# Revit family: Rohrschelle Omnia, M10, Gummi
name_source: partatom
category: HLS-Bauteile
revit_build: Autodesk Revit 2017 (Build: 20190507_1515(x64)
units: mm (PartAtom-declared; Revit-internal decimal feet)

## family parameters
Arbeitsebenenbasiert = Ja
Beim Laden mit Abzugskörper schneiden = Nein
Bemaßung runder Anschluss = Durchmesser verwenden
Gemeinsam genutzt = Ja
Immer vertikal = Nein
Raumberechnungspunkt = Nein
Teiletyp = Normal

## types (10) — shared parameters
Anschluss = M10
BP = 14 mm  [stored 0.0459318 ft]
Bauart = einteilig
Baustoffklasse = B2
DS = 6 mm  [stored 0.019685 ft]
DVS = 5 mm  [stored 0.0164042 ft]
Dämmstärke = 6 mm  [stored 0.019685 ft]
Fabrikat = MEFA
Farbe Schalldämmeinlage = schwarz
Firma = MEFA Befestigungs- und Montagesysteme GmbH
HGA = 14 mm  [stored 0.0459318 ft]
MB = 20 mm  [stored 0.0656168 ft]
Material = Stahl
Material Schalldämmeinlage = TPE
Materialname = DC01-A, DD11
Mengeneinheit = St
Oberflaeche = galvanisch verzinkt
Schalldämmeinlage = Gummi
Verschluss = Schwenkbarer U-Verschluss
Verschluss-Schraube = M6
Vorgabe-Ansicht = 1219 mm
max. Temperaturbeständigkeit = 100 °C
max. zul. Last horizontal = 0.00 kN
max. zul. Last vertikal = 0.00 kN
zero-valued in all types: Nennweite DN Rohr, Stärke Material

## per-type parameters (varying)
- Omnia, Ø 15- 17, M10, Gummi: A=21 mm  [stored 0.0688976 ft]; Anschlußhöhe=21 mm; Artikelnummer=0381152; B=39 mm  [stored 0.127953 ft]; Breite=39 mm  [stored 0.127953 ft]; D=17 mm; D0=29 mm  [stored 0.0951444 ft]; DF1=4 mm  [stored 0.0131234 ft]; DF2=5 mm  [stored 0.0164042 ft]; Dmax=17 mm; EAN=4250928407979; Gewicht=0.05 kg; Gewicht pro Bauteil=0.05 kg; H=45 mm  [stored 0.147638 ft]; Höhe=42 mm; Kurztext1=Rohrschelle Omnia 20x0,8; Kurztext2=15 - 17 mm M10 TPE; MD=1 mm  [stored 0.00328084 ft]; Materialmaße=20x0,8 mm; R=9 mm  [stored 0.0295276 ft]; RM=15 mm  [stored 0.0492126 ft]; Rohraußendurchmesser=0 mm  [stored 0 ft]; Rohraußendurchmesser Zoll=Zoll; max. Höhe=42 mm  [stored 0.137795 ft]; max. Rohraußendurchmesser=17 mm; max. zul. Last=0.80 kN; min. Rohraußendurchmesser=15 mm  [stored 0.0492126 ft]; vpe=100 St
- Omnia, Ø 18- 20, M10, Gummi: A=21 mm  [stored 0.0688976 ft]; Anschlußhöhe=21 mm; Artikelnummer=0381187; B=43 mm  [stored 0.141076 ft]; Breite=43 mm  [stored 0.141076 ft]; D=20 mm  [stored 0.0656168 ft]; D0=32 mm  [stored 0.104987 ft]; DF1=5 mm  [stored 0.0164042 ft]; DF2=5 mm  [stored 0.0164042 ft]; Dmax=20 mm  [stored 0.0656168 ft]; EAN=4250928407986; Gewicht=0.05 kg; Gewicht pro Bauteil=0.05 kg; H=48 mm  [stored 0.15748 ft]; Höhe=45 mm; Kurztext1=Rohrschelle Omnia 20x0,8; Kurztext2=18 - 20 mm M10 TPE; MD=1 mm  [stored 0.00328084 ft]; Materialmaße=20x0,8 mm; R=10 mm  [stored 0.0328084 ft]; RM=17 mm; Rohraußendurchmesser=0 mm  [stored 0 ft]; Rohraußendurchmesser Zoll=3/8 Zoll; max. Höhe=45 mm  [stored 0.147638 ft]; max. Rohraußendurchmesser=20 mm  [stored 0.0656168 ft]; max. zul. Last=0.80 kN; min. Rohraußendurchmesser=18 mm  [stored 0.0590551 ft]; vpe=100 St
- Omnia, Ø 22- 24, M10, Gummi: A=21 mm  [stored 0.0688976 ft]; Anschlußhöhe=21 mm; Artikelnummer=0381225; B=47 mm  [stored 0.154199 ft]; Breite=47 mm  [stored 0.154199 ft]; D=24 mm  [stored 0.0787402 ft]; D0=36 mm  [stored 0.11811 ft]; DF1=5 mm  [stored 0.0164042 ft]; DF2=5 mm  [stored 0.0164042 ft]; Dmax=24 mm  [stored 0.0787402 ft]; EAN=4250928407993; Gewicht=0.06 kg; Gewicht pro Bauteil=0.06 kg; H=52 mm; Höhe=48 mm; Kurztext1=Rohrschelle Omnia 20x0,8; Kurztext2=22 - 24 mm M10 TPE; MD=1 mm  [stored 0.00328084 ft]; Materialmaße=20x0,8 mm; R=12 mm  [stored 0.0393701 ft]; RM=19 mm; Rohraußendurchmesser=0 mm  [stored 0 ft]; Rohraußendurchmesser Zoll=1/2 Zoll; max. Höhe=48 mm  [stored 0.15748 ft]; max. Rohraußendurchmesser=24 mm  [stored 0.0787402 ft]; max. zul. Last=0.80 kN; min. Rohraußendurchmesser=22 mm  [stored 0.0721785 ft]; vpe=100 St
- Omnia, Ø 28- 30, M10, Gummi: A=21 mm  [stored 0.0688976 ft]; Anschlußhöhe=21 mm; Artikelnummer=0381284; B=55 mm; Breite=55 mm; D=30 mm  [stored 0.0984252 ft]; D0=42 mm  [stored 0.137795 ft]; DF1=6 mm  [stored 0.019685 ft]; DF2=6 mm  [stored 0.019685 ft]; Dmax=30 mm  [stored 0.0984252 ft]; EAN=4250928408006; Gewicht=0.06 kg; Gewicht pro Bauteil=0.06 kg; H=58 mm; Höhe=54 mm; Kurztext1=Rohrschelle Omnia 20x0,8; Kurztext2=28 - 30 mm M10 TPE; MD=1 mm  [stored 0.00328084 ft]; Materialmaße=20x0,8 mm; R=15 mm  [stored 0.0492126 ft]; RM=22 mm  [stored 0.0721785 ft]; Rohraußendurchmesser=0 mm  [stored 0 ft]; Rohraußendurchmesser Zoll=3/4 Zoll; max. Höhe=54 mm; max. Rohraußendurchmesser=30 mm  [stored 0.0984252 ft]; max. zul. Last=0.80 kN; min. Rohraußendurchmesser=28 mm  [stored 0.0918635 ft]; vpe=100 St
- Omnia, Ø 35- 37, M10, Gummi: A=21 mm  [stored 0.0688976 ft]; Anschlußhöhe=21 mm; Artikelnummer=0381357; B=61 mm; Breite=61 mm; D=37 mm  [stored 0.121391 ft]; D0=49 mm  [stored 0.160761 ft]; DF1=5 mm  [stored 0.0164042 ft]; DF2=6 mm  [stored 0.019685 ft]; Dmax=37 mm  [stored 0.121391 ft]; EAN=4250928408013; Gewicht=0.07 kg; Gewicht pro Bauteil=0.07 kg; H=65 mm; Höhe=62 mm; Kurztext1=Rohrschelle Omnia 20x1,0; Kurztext2=35 - 37 mm M10 TPE; MD=1 mm  [stored 0.00328084 ft]; Materialmaße=20x1,0 mm; R=19 mm; RM=26 mm; Rohraußendurchmesser=0 mm  [stored 0 ft]; Rohraußendurchmesser Zoll=1 Zoll; max. Höhe=62 mm; max. Rohraußendurchmesser=37 mm  [stored 0.121391 ft]; max. zul. Last=1.00 kN; min. Rohraußendurchmesser=35 mm  [stored 0.114829 ft]; vpe=100 St
- Omnia, Ø 42- 43, M10, Gummi: A=21 mm  [stored 0.0688976 ft]; Anschlußhöhe=21 mm; Artikelnummer=0381411; B=68 mm; Breite=68 mm; D=43 mm  [stored 0.141076 ft]; D0=55 mm; DF1=6 mm  [stored 0.019685 ft]; DF2=6 mm  [stored 0.019685 ft]; Dmax=43 mm  [stored 0.141076 ft]; EAN=4250928408020; Gewicht=0.08 kg; Gewicht pro Bauteil=0.08 kg; H=71 mm; Höhe=69 mm; Kurztext1=Rohrschelle Omnia 20x1,0; Kurztext2=42 - 43 mm M10 TPE; MD=1 mm  [stored 0.00328084 ft]; Materialmaße=20x1,0 mm; R=22 mm  [stored 0.0721785 ft]; RM=29 mm  [stored 0.0951444 ft]; Rohraußendurchmesser=0 mm  [stored 0 ft]; Rohraußendurchmesser Zoll=1 1/4 Zoll; max. Höhe=69 mm; max. Rohraußendurchmesser=43 mm  [stored 0.141076 ft]; max. zul. Last=1.00 kN; min. Rohraußendurchmesser=42 mm  [stored 0.137795 ft]; vpe=50 St
- Omnia, Ø 48- 49, M10, Gummi: A=21 mm  [stored 0.0688976 ft]; Anschlußhöhe=21 mm; Artikelnummer=0381489; B=75 mm; Breite=75 mm; D=49 mm  [stored 0.160761 ft]; D0=61 mm; DF1=6 mm  [stored 0.019685 ft]; DF2=7 mm  [stored 0.0229659 ft]; Dmax=49 mm  [stored 0.160761 ft]; EAN=4250928408044; Gewicht=0.08 kg; Gewicht pro Bauteil=0.08 kg; H=77 mm; Höhe=75 mm; Kurztext1=Rohrschelle Omnia 20x1,0; Kurztext2=48 - 49 mm M10 TPE; MD=1 mm  [stored 0.00328084 ft]; Materialmaße=20x1,0 mm; R=25 mm  [stored 0.082021 ft]; RM=32 mm  [stored 0.104987 ft]; Rohraußendurchmesser=0 mm  [stored 0 ft]; Rohraußendurchmesser Zoll=1 1/2 Zoll; max. Höhe=75 mm; max. Rohraußendurchmesser=49 mm  [stored 0.160761 ft]; max. zul. Last=1.00 kN; min. Rohraußendurchmesser=48 mm  [stored 0.15748 ft]; vpe=50 St
- Omnia, Ø 50- 52, M10, Gummi: A=22 mm  [stored 0.0721785 ft]; Anschlußhöhe=22 mm; Artikelnummer=0381519; B=85 mm; Breite=85 mm; D=52 mm; D0=64 mm; DF1=10 mm  [stored 0.0328084 ft]; DF2=10 mm  [stored 0.0328084 ft]; Dmax=52 mm; EAN=4250928408051; Gewicht=0.11 kg; Gewicht pro Bauteil=0.11 kg; H=81 mm; Höhe=80 mm; Kurztext1=Rohrschelle Omnia 20x1,5; Kurztext2=50 - 52 mm M10 TPE; MD=2 mm  [stored 0.00656168 ft]; Materialmaße=20x1,5 mm; R=26 mm; RM=34 mm; Rohraußendurchmesser=0 mm  [stored 0 ft]; Rohraußendurchmesser Zoll=Zoll; max. Höhe=80 mm; max. Rohraußendurchmesser=52 mm; max. zul. Last=1.20 kN; min. Rohraußendurchmesser=50 mm  [stored 0.164042 ft]; vpe=50 St
- Omnia, Ø 54, M10, Gummi: A=22 mm  [stored 0.0721785 ft]; Anschlußhöhe=22 mm; Artikelnummer=0381543; B=89 mm; Breite=89 mm; D=54 mm; D0=66 mm; DF1=11 mm  [stored 0.0360892 ft]; DF2=11 mm  [stored 0.0360892 ft]; Dmax=54 mm; EAN=4250928408068; Gewicht=0.12 kg; Gewicht pro Bauteil=0.12 kg; H=83 mm; Höhe=82 mm; Kurztext1=Rohrschelle Omnia 20x1,5; Kurztext2=54 mm M10 TPE; MD=2 mm  [stored 0.00656168 ft]; Materialmaße=20x1,5 mm; R=27 mm  [stored 0.0885827 ft]; RM=35 mm  [stored 0.114829 ft]; Rohraußendurchmesser=54 mm; Rohraußendurchmesser Zoll=Zoll; max. Höhe=82 mm; max. Rohraußendurchmesser=0 mm  [stored 0 ft]; max. zul. Last=1.20 kN; min. Rohraußendurchmesser=0 mm  [stored 0 ft]; vpe=50 St
- Omnia, Ø 57, M10, Gummi: A=22 mm  [stored 0.0721785 ft]; Anschlußhöhe=22 mm; Artikelnummer=0381578; B=91 mm; Breite=91 mm; D=57 mm; D0=69 mm; DF1=10 mm  [stored 0.0328084 ft]; DF2=11 mm  [stored 0.0360892 ft]; Dmax=57 mm; EAN=4250928408075; Gewicht=0.12 kg; Gewicht pro Bauteil=0.12 kg; H=86 mm; Höhe=86 mm; Kurztext1=Rohrschelle Omnia 20x1,5; Kurztext2=57 mm M10 TPE; MD=2 mm  [stored 0.00656168 ft]; Materialmaße=20x1,5 mm; R=29 mm  [stored 0.0951444 ft]; RM=36 mm  [stored 0.11811 ft]; Rohraußendurchmesser=57 mm; Rohraußendurchmesser Zoll=Zoll; max. Höhe=86 mm; max. Rohraußendurchmesser=0 mm  [stored 0 ft]; max. zul. Last=1.20 kN; min. Rohraußendurchmesser=0 mm  [stored 0 ft]; vpe=50 St

note: [stored X ft] marks values corroborated as IEEE doubles in the binary element streams (Revit-internal decimal feet)

## geometry (parser evidence)
native form markers: Sweep x3
no freeform markers — native parametric forms only
